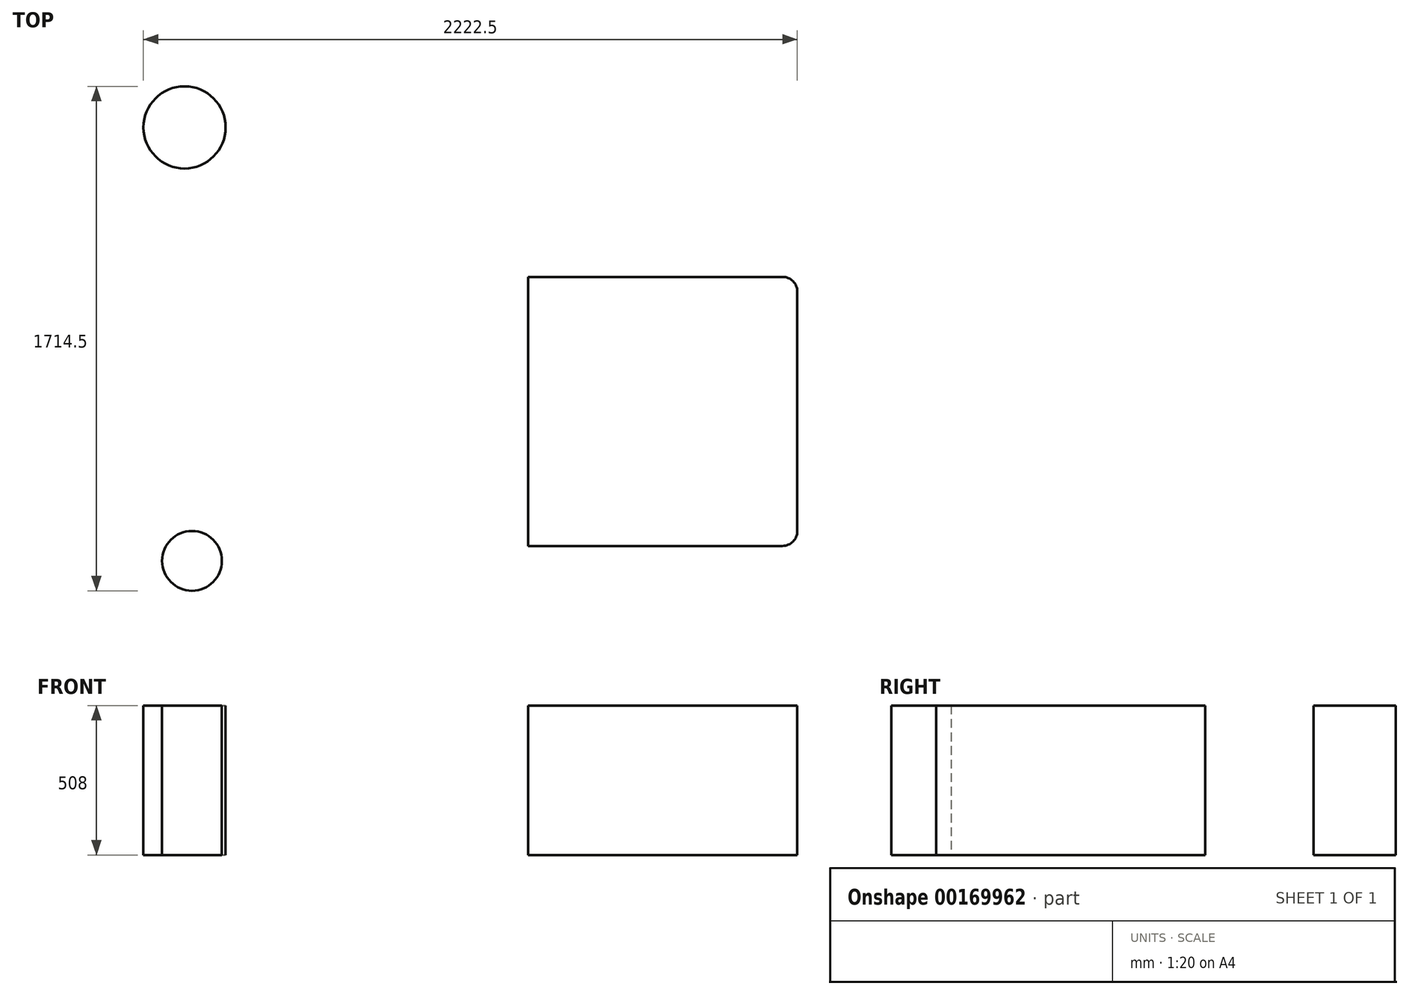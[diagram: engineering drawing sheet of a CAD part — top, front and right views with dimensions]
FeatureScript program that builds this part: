
annotation { "Feature Type Name" : "Feature", "Feature Type Description" : "" }
export const myFeature = defineFeature(function(context is Context, id is Id, definition is map)
    precondition{}
    {
        {
            var Q0;
            Q0=qCreatedBy(makeId("Top.planeOp"),FACE);
            var sketch = newSketch(context, id + "F0", { "sketchPlane" : qUnion([Q0])});
            skLineSegment(sketch, "E0.bottom", {"start": v(406.4, 457.2) * mm, "end": v(-457.2, 457.2) * mm});
            skLineSegment(sketch, "E0.top", {"start": v(406.4, -457.2) * mm, "end": v(-457.2, -457.2) * mm});
            skLineSegment(sketch, "E0.left", {"start": v(457.2, 406.4) * mm, "end": v(457.2, -406.4) * mm});
            skLineSegment(sketch, "E0.right", {"start": v(-457.2, 457.2) * mm, "end": v(-457.2, -457.2) * mm});
            skPoint(sketch, "E0.middle", {"position": v(0, 0) * mm});
            skPoint(sketch, "E1.visualSharp", {"position": v(457.2, 457.2) * mm});
            skArc(sketch, "E1.filletArc", {"start": v(457.2, 406.4) * mm, "mid": v(442.32, 442.32) * mm, "end": v(406.4, 457.2) * mm});
            skPoint(sketch, "E2.visualSharp", {"position": v(457.2, -457.2) * mm});
            skArc(sketch, "E2.filletArc", {"start": v(406.4, -457.2) * mm, "mid": v(442.32, -442.32) * mm, "end": v(457.2, -406.4) * mm});
            skSolve(sketch);
        }
        {
            var Q0;
            Q0 = qSketchRegion(id + "F0", true);
            extrude(context, id + "F1", {"entities" : qUnion([Q0]), "depth" : 508 * mm});
        }
        {
            var Q0;
            Q0=qCreatedBy(makeId("Top.planeOp"),FACE);
            var sketch = newSketch(context, id + "F2", { "sketchPlane" : qUnion([Q0])});
            skCircle(sketch, "E3", {"center": v(-1600.2, -508) * mm, "radius": 101.6 * mm});
            skSolve(sketch);
        }
        {
            var Q0;
            Q0 = qSketchRegion(id + "F2", true);
            extrude(context, id + "F3", {"entities" : qUnion([Q0]), "depth" : 508 * mm});
        }
        {
            var Q0;
            Q0=qCreatedBy(makeId("Top.planeOp"),FACE);
            var sketch = newSketch(context, id + "F4", { "sketchPlane" : qUnion([Q0])});
            skCircle(sketch, "E4", {"center": v(-1625.6, 965.2) * mm, "radius": 139.7 * mm});
            skSolve(sketch);
        }
        {
            var Q0;
            Q0 = qSketchRegion(id + "F4", true);
            extrude(context, id + "F5", {"entities" : qUnion([Q0]), "depth" : 508 * mm});
        }
    });
